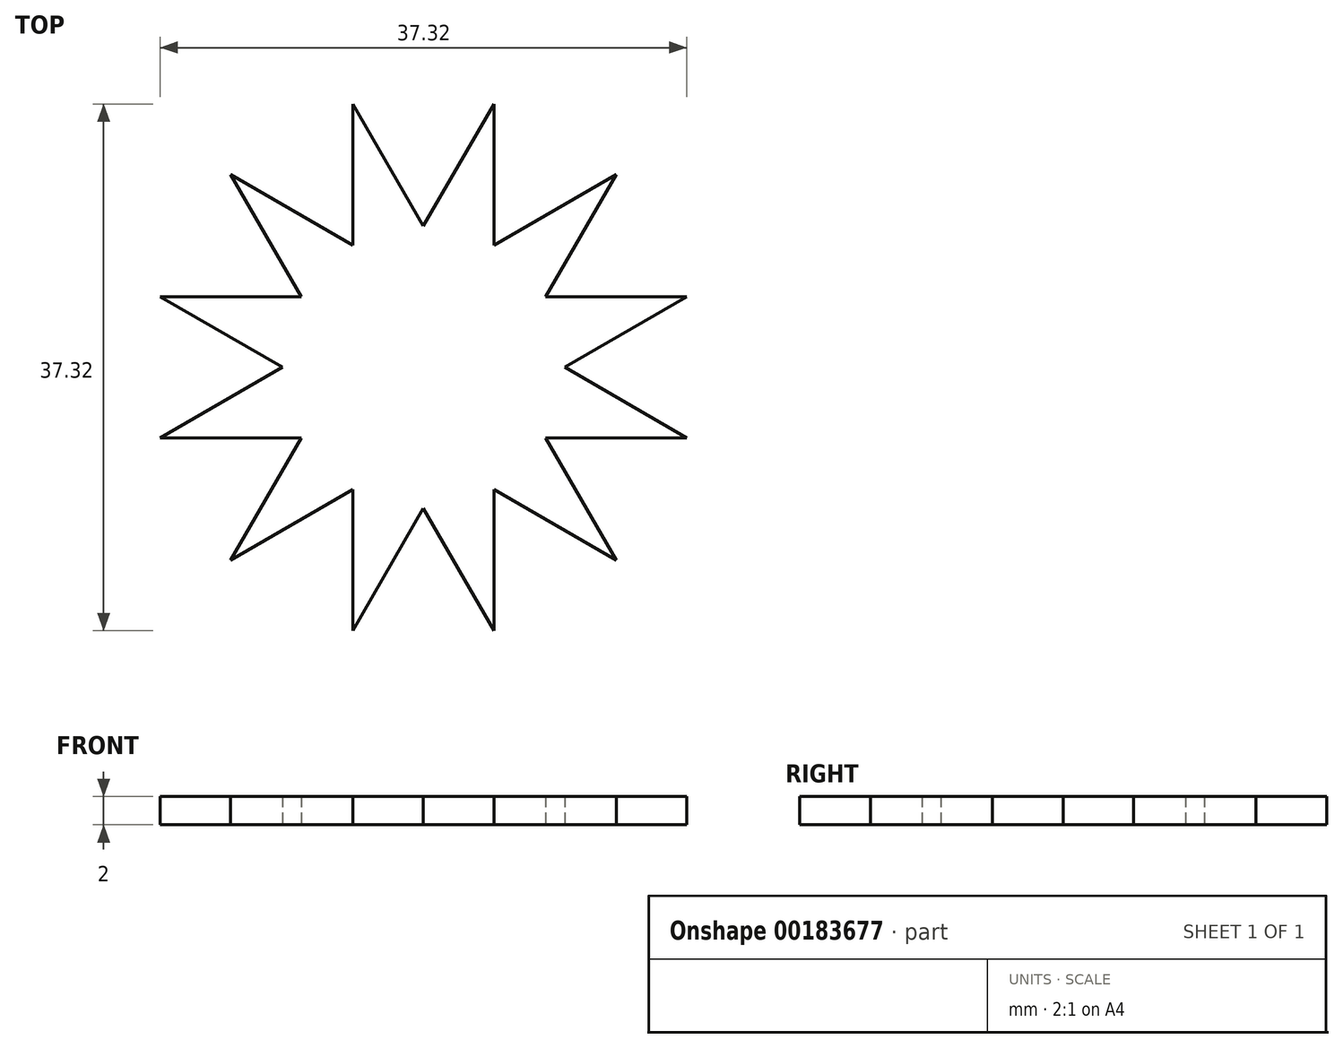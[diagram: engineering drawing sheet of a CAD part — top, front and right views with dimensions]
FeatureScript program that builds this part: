
annotation { "Feature Type Name" : "Feature", "Feature Type Description" : "" }
export const myFeature = defineFeature(function(context is Context, id is Id, definition is map)
    precondition{}
    {
        {
            var Q0;
            Q0=qCreatedBy(makeId("Top.planeOp"),FACE);
            var sketch = newSketch(context, id + "F0", { "sketchPlane" : qUnion([Q0])});
            skLineSegment(sketch, "E0", {"start": v(-5, 18.66) * mm, "end": v(0, 10) * mm});
            skLineSegment(sketch, "E1", {"start": v(0, 10) * mm, "end": v(5, 18.66) * mm});
            skLineSegment(sketch, "E2", {"start": v(5, 18.66) * mm, "end": v(5, 8.66) * mm});
            skLineSegment(sketch, "E3", {"start": v(5, 8.66) * mm, "end": v(13.66, 13.66) * mm});
            skLineSegment(sketch, "E4", {"start": v(13.66, 13.66) * mm, "end": v(8.66, 5) * mm});
            skLineSegment(sketch, "E5", {"start": v(8.66, 5) * mm, "end": v(18.66, 5) * mm});
            skLineSegment(sketch, "E6", {"start": v(18.66, 5) * mm, "end": v(10, 0) * mm});
            skLineSegment(sketch, "E7", {"start": v(10, 0) * mm, "end": v(18.66, -5) * mm});
            skLineSegment(sketch, "E8", {"start": v(18.66, -5) * mm, "end": v(8.66, -5) * mm});
            skLineSegment(sketch, "E9", {"start": v(8.66, -5) * mm, "end": v(13.66, -13.66) * mm});
            skLineSegment(sketch, "E10", {"start": v(13.66, -13.66) * mm, "end": v(5, -8.66) * mm});
            skLineSegment(sketch, "E11", {"start": v(5, -8.66) * mm, "end": v(5, -18.66) * mm});
            skLineSegment(sketch, "E12", {"start": v(5, -18.66) * mm, "end": v(0, -10) * mm});
            skLineSegment(sketch, "E13", {"start": v(0, -10) * mm, "end": v(-5, -18.66) * mm});
            skLineSegment(sketch, "E14", {"start": v(-5, -18.66) * mm, "end": v(-5, -8.66) * mm});
            skLineSegment(sketch, "E15", {"start": v(-5, -8.66) * mm, "end": v(-13.66, -13.66) * mm});
            skLineSegment(sketch, "E16", {"start": v(-13.66, -13.66) * mm, "end": v(-8.66, -5) * mm});
            skLineSegment(sketch, "E17", {"start": v(-8.66, -5) * mm, "end": v(-18.66, -5) * mm});
            skLineSegment(sketch, "E18", {"start": v(-18.66, -5) * mm, "end": v(-10, 0) * mm});
            skLineSegment(sketch, "E19", {"start": v(-10, 0) * mm, "end": v(-18.66, 5) * mm});
            skLineSegment(sketch, "E20", {"start": v(-18.66, 5) * mm, "end": v(-8.66, 5) * mm});
            skLineSegment(sketch, "E21", {"start": v(-8.66, 5) * mm, "end": v(-13.66, 13.66) * mm});
            skLineSegment(sketch, "E22", {"start": v(-13.66, 13.66) * mm, "end": v(-5, 8.66) * mm});
            skLineSegment(sketch, "E23", {"start": v(-5, 8.66) * mm, "end": v(-5, 18.66) * mm});
            skCircle(sketch, "E24", {"center": v(0, 0) * mm, "radius": 19.32 * mm, "construction": true});
            skCircle(sketch, "E25", {"center": v(0, 0) * mm, "radius": 10 * mm, "construction": true});
            skSolve(sketch);
        }
        {
            var Q0;
            Q0 = qSketchRegion(id + "F0", true);
            extrude(context, id + "F1", {"entities" : qUnion([Q0]), "depth" : 2 * mm});
        }
    });
